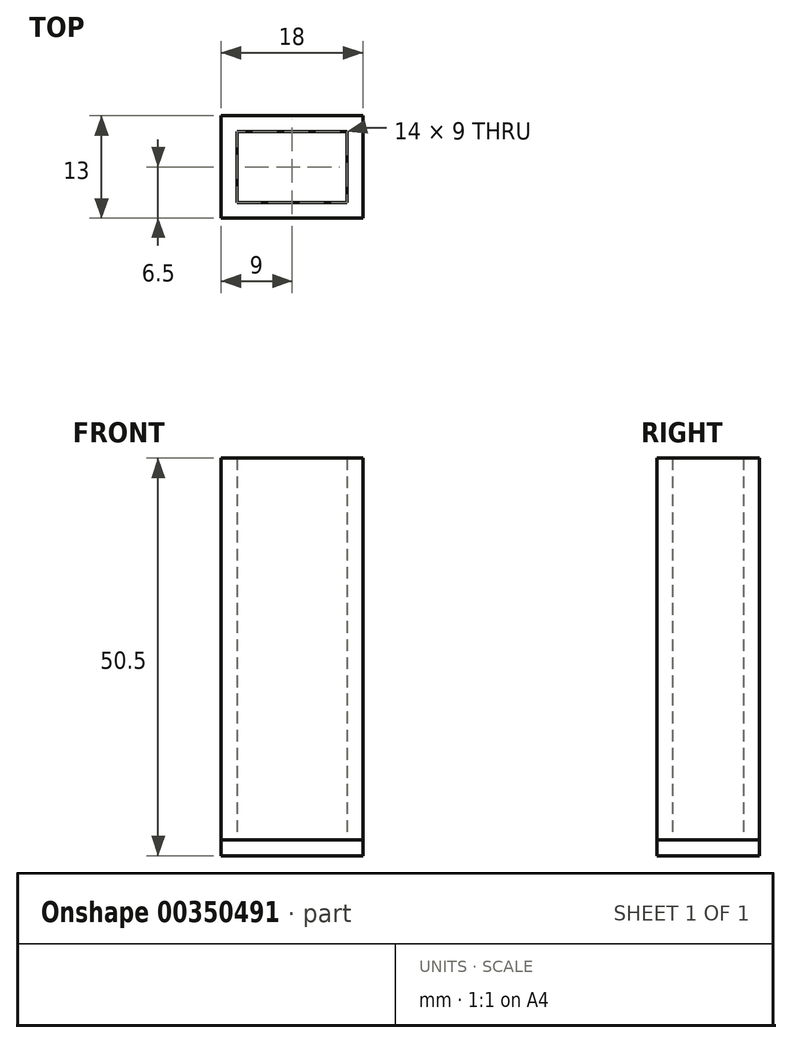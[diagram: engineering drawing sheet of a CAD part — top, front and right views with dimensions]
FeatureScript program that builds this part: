
annotation { "Feature Type Name" : "Feature", "Feature Type Description" : "" }
export const myFeature = defineFeature(function(context is Context, id is Id, definition is map)
    precondition{}
    {
        {
            var Q0;
            Q0=qCreatedBy(makeId("Top.planeOp"),FACE);
            var sketch = newSketch(context, id + "F0", { "sketchPlane" : qUnion([Q0])});
            skLineSegment(sketch, "E0", {"start": v(7, 4.5) * mm, "end": v(7, -4.5) * mm});
            skLineSegment(sketch, "E1", {"start": v(7, -4.5) * mm, "end": v(-7, -4.5) * mm});
            skLineSegment(sketch, "E2", {"start": v(-7, -4.5) * mm, "end": v(-7, 4.5) * mm});
            skLineSegment(sketch, "E3", {"start": v(-7, 4.5) * mm, "end": v(7, 4.5) * mm});
            skLineSegment(sketch, "E4.bottom", {"start": v(-9, 6.5) * mm, "end": v(9, 6.5) * mm});
            skLineSegment(sketch, "E4.top", {"start": v(-9, -6.5) * mm, "end": v(9, -6.5) * mm});
            skLineSegment(sketch, "E4.left", {"start": v(-9, 6.5) * mm, "end": v(-9, -6.5) * mm});
            skLineSegment(sketch, "E4.right", {"start": v(9, 6.5) * mm, "end": v(9, -6.5) * mm});
            skSolve(sketch);
        }
        {
            var Q0;
            Q0 = qSketchRegion(id + "F0", true);
            extrude(context, id + "F1", {"entities" : qUnion([Q0]), "depth" : 48.5 * mm, "offsetDistance" : 25 * mm});
        }
        {
            var Q0;
            Q0=makeQuery(id+"F0.imprint","IMPRINT",FACE,{"disambiguationData":[TD([[makeQuery(id+"F0.imprint","IMPRINT",EDGE,{"derivedFrom":sQuery(id+"F0.wireOp",EDGE,"E0")}),-1.0]])]});
            var Q1;
            Q1=makeQuery(id+"F0.imprint","IMPRINT",FACE,{"disambiguationData":[TD([[makeQuery(id+"F0.imprint","IMPRINT",EDGE,{"derivedFrom":sQuery(id+"F0.wireOp",EDGE,"E0")}),1.0]])]});
            var Q2;
            Q2=sQuery(id+"F0.wireOp",EDGE,"E4.left");
            var Q3;
            Q3=sQuery(id+"F0.wireOp",EDGE,"E4.top");
            var Q4;
            Q4=sQuery(id+"F0.wireOp",EDGE,"E4.right");
            var Q5;
            Q5=sQuery(id+"F0.wireOp",EDGE,"E4.bottom");
            extrude(context, id + "F2", {"entities" : qUnion([Q0, Q1]), "surfaceEntities" : qUnion([Q2, Q3, Q4, Q5]), "depth" : -2 * mm, "offsetDistance" : 25 * mm});
        }
    });
